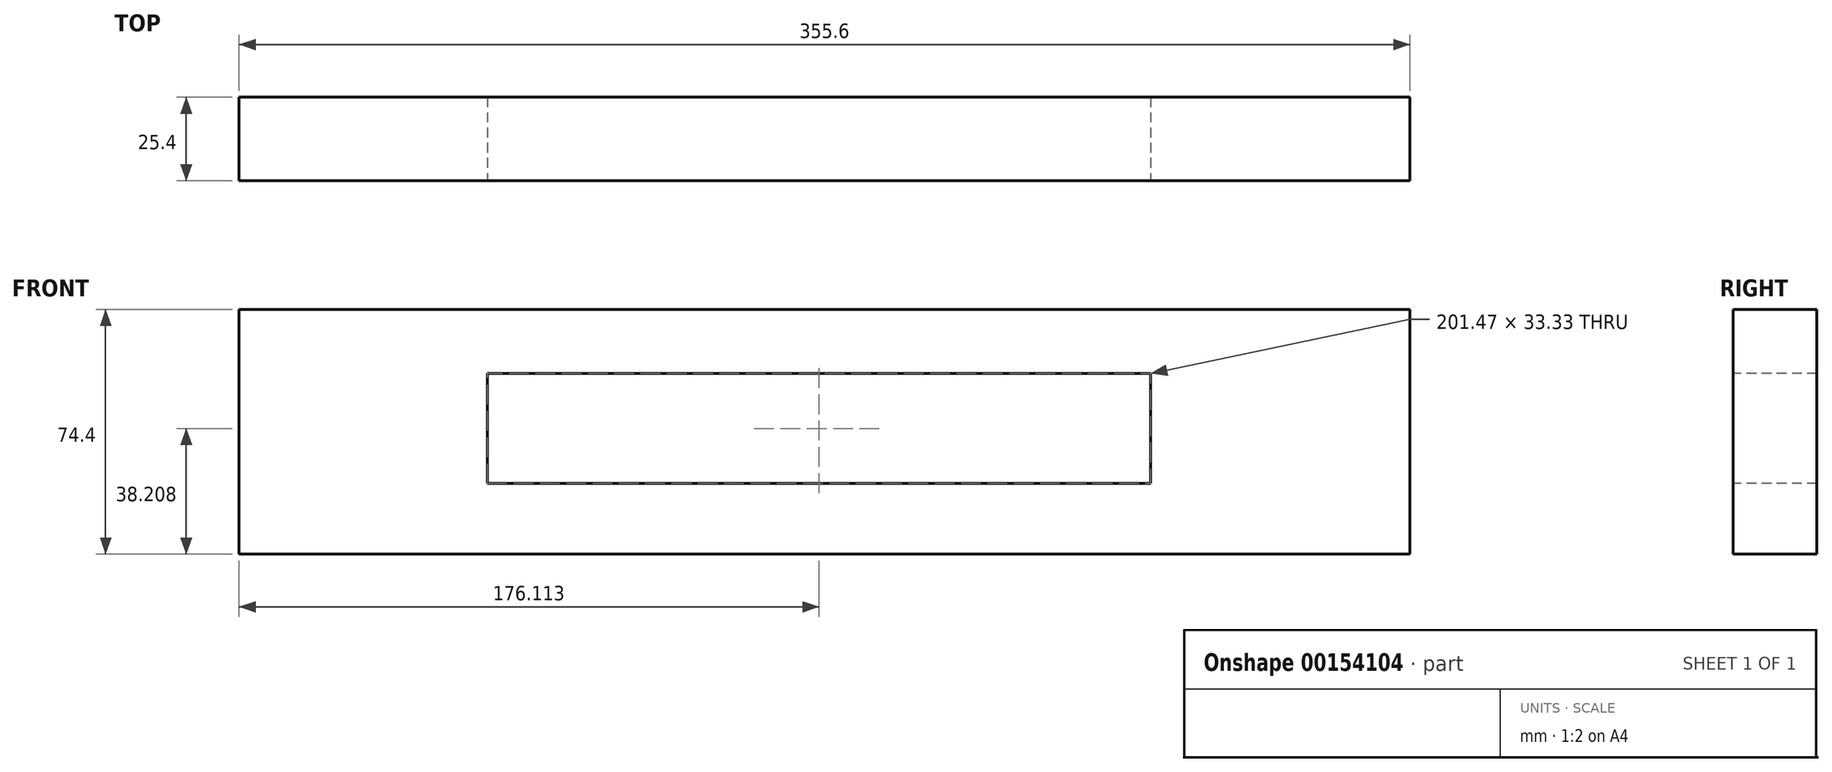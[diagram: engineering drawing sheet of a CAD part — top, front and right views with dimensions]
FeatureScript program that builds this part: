
annotation { "Feature Type Name" : "Feature", "Feature Type Description" : "" }
export const myFeature = defineFeature(function(context is Context, id is Id, definition is map)
    precondition{}
    {
        {
            var Q0;
            Q0=qCreatedBy(makeId("Front.planeOp"),FACE);
            var sketch = newSketch(context, id + "F0", { "sketchPlane" : qUnion([Q0])});
            skLineSegment(sketch, "E0.bottom", {"start": v(-181.43, 83.23) * mm, "end": v(174.17, 83.23) * mm});
            skLineSegment(sketch, "E0.top", {"start": v(-181.43, 8.83) * mm, "end": v(174.17, 8.83) * mm});
            skLineSegment(sketch, "E0.left", {"start": v(-181.43, 83.23) * mm, "end": v(-181.43, 8.83) * mm});
            skLineSegment(sketch, "E0.right", {"start": v(174.17, 83.23) * mm, "end": v(174.17, 8.83) * mm});
            skLineSegment(sketch, "E1.bottom", {"start": v(-181.43, 8.83) * mm, "end": v(-127.82, 8.83) * mm});
            skLineSegment(sketch, "E2.bottom", {"start": v(123.84, 8.83) * mm, "end": v(173.08, 8.83) * mm});
            skSolve(sketch);
        }
        {
            var Q0;
            Q0=makeQuery(id+"F0.imprint","IMPRINT",FACE,{"disambiguationData":[TD([[makeQuery(id+"F0.imprint","IMPRINT",EDGE,{"derivedFrom":sQuery(id+"F0.wireOp",EDGE,"E0.bottom")}),-1.0]])]});
            extrude(context, id + "F1", {"entities" : qUnion([Q0]), "depth" : 25.4 * mm, "offsetDistance" : 25.4 * mm});
        }
        {
            var Q0;
            Q0=makeQuery(id+"F1.opExtrude","CAP_FACE",FACE,{"disambiguationData":[OSD([sQuery(id+"F0.wireOp",EDGE,"E0.bottom"),sQuery(id+"F0.wireOp",EDGE,"E0.top"),sQuery(id+"F0.wireOp",EDGE,"E0.left"),sQuery(id+"F0.wireOp",EDGE,"E0.right"),sQuery(id+"F0.wireOp",EDGE,"E1.bottom"),sQuery(id+"F0.wireOp",EDGE,"E2.bottom")])],"isStart":false});
            var sketch = newSketch(context, id + "F2", { "sketchPlane" : qUnion([Q0])});
            skLineSegment(sketch, "E3.bottom", {"start": v(-106.05, 63.7) * mm, "end": v(95.42, 63.7) * mm});
            skLineSegment(sketch, "E3.top", {"start": v(-106.05, 30.37) * mm, "end": v(95.42, 30.37) * mm});
            skLineSegment(sketch, "E3.left", {"start": v(-106.05, 63.7) * mm, "end": v(-106.05, 30.37) * mm});
            skLineSegment(sketch, "E3.right", {"start": v(95.42, 63.7) * mm, "end": v(95.42, 30.37) * mm});
            skSolve(sketch);
        }
        {
            var Q0;
            Q0=makeQuery(id+"F2.imprint","IMPRINT",FACE,{"disambiguationData":[TD([[makeQuery(id+"F2.imprint","IMPRINT",EDGE,{"derivedFrom":sQuery(id+"F2.wireOp",EDGE,"E3.bottom")}),1.0]])]});
            extrude(context, id + "F3", {"entities" : qUnion([Q0]), "operationType" : NewBodyOperationType.INTERSECT, "oppositeDirection" : true, "depth" : 25.4 * mm, "offsetDistance" : 25.4 * mm});
        }
    });
